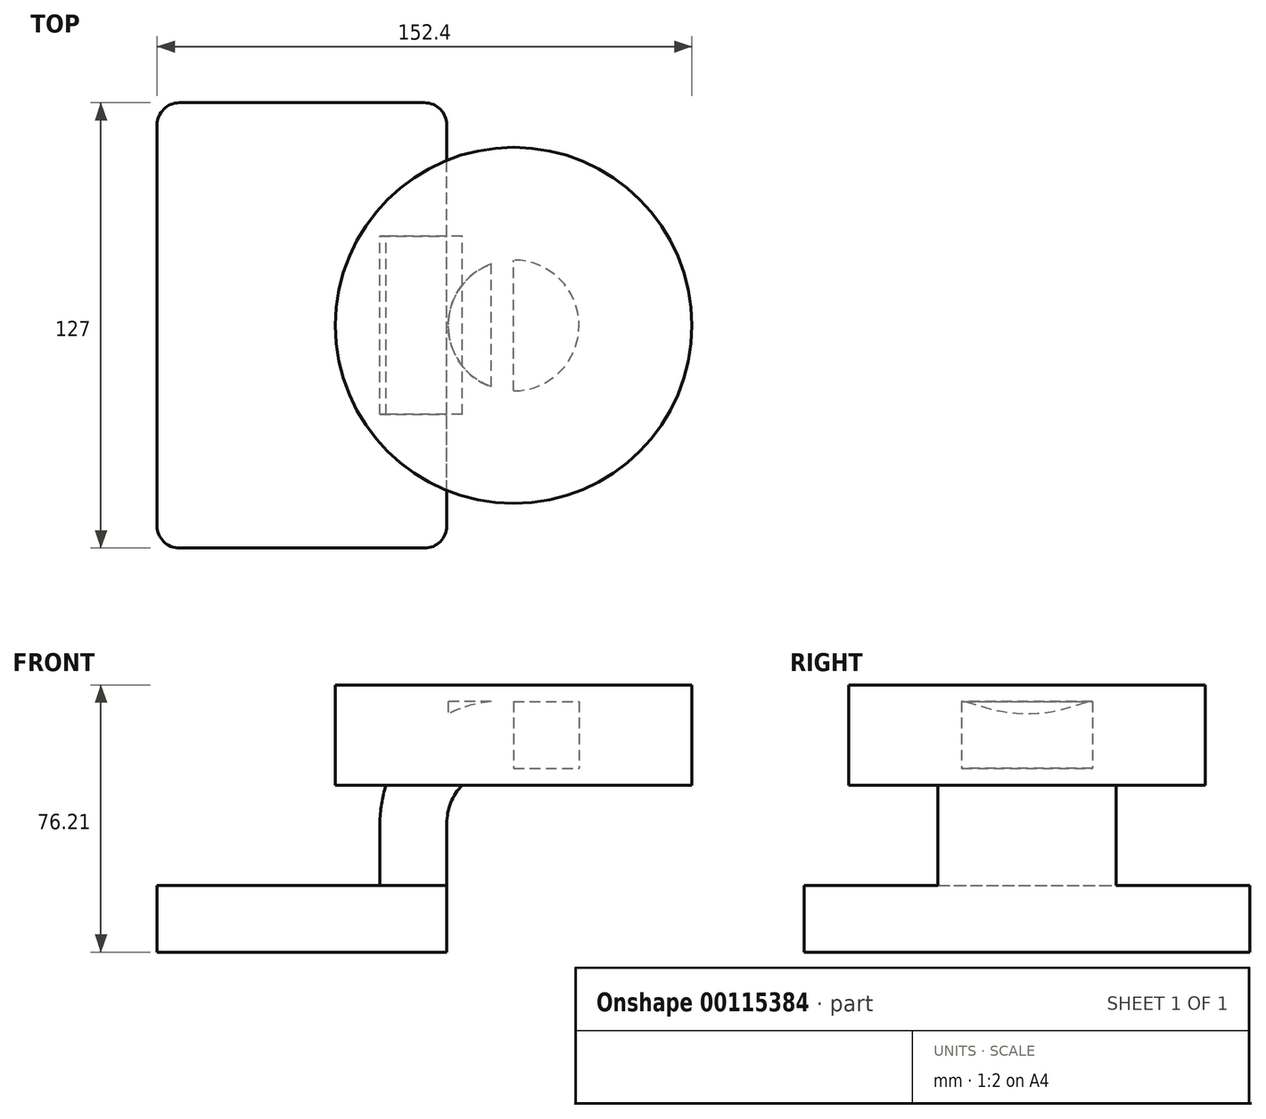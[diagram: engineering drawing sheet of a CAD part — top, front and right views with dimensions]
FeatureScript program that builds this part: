
annotation { "Feature Type Name" : "Feature", "Feature Type Description" : "" }
export const myFeature = defineFeature(function(context is Context, id is Id, definition is map)
    precondition{}
    {
        {
            var Q0;
            Q0=qCreatedBy(makeId("Front.planeOp"),FACE);
            var sketch = newSketch(context, id + "F0", { "sketchPlane" : qUnion([Q0])});
            skLineSegment(sketch, "E0.bottom", {"start": v(-41.28, 9.52) * mm, "end": v(41.28, 9.53) * mm});
            skLineSegment(sketch, "E0.top", {"start": v(-41.28, -9.53) * mm, "end": v(41.28, -9.53) * mm});
            skLineSegment(sketch, "E0.left", {"start": v(-41.28, 9.52) * mm, "end": v(-41.28, -9.53) * mm});
            skLineSegment(sketch, "E0.right", {"start": v(41.28, 9.53) * mm, "end": v(41.28, -9.52) * mm});
            skPoint(sketch, "E0.middle", {"position": v(0, 0) * mm});
            skLineSegment(sketch, "E1.bottom", {"start": v(111.12, 38.1) * mm, "end": v(60.32, 38.1) * mm});
            skLineSegment(sketch, "E1.top", {"start": v(111.12, 66.68) * mm, "end": v(60.32, 66.68) * mm});
            skLineSegment(sketch, "E1.left", {"start": v(111.12, 38.1) * mm, "end": v(111.12, 66.68) * mm});
            skLineSegment(sketch, "E1.right", {"start": v(60.32, 38.1) * mm, "end": v(60.32, 66.68) * mm});
            skPoint(sketch, "E1.middle", {"position": v(85.72, 52.39) * mm});
            skLineSegment(sketch, "E2", {"start": v(41.27, 9.53) * mm, "end": v(41.27, 27.15) * mm});
            skArc(sketch, "E3", {"start": v(41.27, 27.15) * mm, "mid": v(45.19, 37.58) * mm, "end": v(55, 42.88) * mm});
            skLineSegment(sketch, "E4", {"start": v(55, 42.88) * mm, "end": v(78.97, 42.88) * mm});
            skLineSegment(sketch, "E5.0", {"start": v(53.95, 61.93) * mm, "end": v(78.97, 61.93) * mm});
            skArc(sketch, "E5.1", {"start": v(22.22, 27.15) * mm, "mid": v(31.35, 50.68) * mm, "end": v(53.95, 61.93) * mm});
            skLineSegment(sketch, "E5.2", {"start": v(22.22, 9.53) * mm, "end": v(22.22, 27.15) * mm});
            skLineSegment(sketch, "E6", {"start": v(78.97, 42.88) * mm, "end": v(78.97, 61.93) * mm});
            skFitSpline(sketch, "E7", {"points": [v(-41.28, 9.52) * mm, v(53.95, 61.93) * mm], "startDerivative": vector(3.25, 108.48) * mm, "endDerivative": vector(161.85, 0) * mm});
            skSolve(sketch);
        }
        {
            var Q0;
            Q0=makeQuery(id+"F0.imprint","IMPRINT",FACE,{"disambiguationData":[TD([[makeQuery(id+"F0.imprint","IMPRINT",EDGE,{"derivedFrom":sQuery(id+"F0.wireOp",EDGE,"E0.top")}),1.0]])]});
            extrude(context, id + "F1", {"entities" : qUnion([Q0]), "endBound" : BoundingType.SYMMETRIC, "depth" : 127 * mm});
        }
        {
            var Q0;
            {var subQ1=sQuery(id+"F0.wireOp",EDGE,"E2");Q0=makeQuery(id+"F0.imprint","IMPRINT",FACE,{"disambiguationData":[TD([[makeQuery(id+"F0.imprint","IMPRINT",EDGE,{"derivedFrom":subQ1}),1.0]])]});}
            extrude(context, id + "F2", {"entities" : qUnion([Q0]), "operationType" : NewBodyOperationType.ADD, "endBound" : BoundingType.SYMMETRIC, "depth" : 50.8 * mm});
        }
        {
            var Q0;
            Q0=makeQuery(id+"F0.imprint","IMPRINT",FACE,{"disambiguationData":[TD([[makeQuery(id+"F0.imprint","IMPRINT",EDGE,{"derivedFrom":sQuery(id+"F0.wireOp",EDGE,"E5.1")}),1.0]])]});
            extrude(context, id + "F3", {"entities" : qUnion([Q0]), "operationType" : NewBodyOperationType.ADD, "endBound" : BoundingType.SYMMETRIC, "depth" : 15.88 * mm});
        }
        {
            var Q0;
            {var subQ1=sQuery(id+"F0.wireOp",EDGE,"E1.bottom");Q0=makeQuery(id+"F0.imprint","IMPRINT",FACE,{"disambiguationData":[TD([[makeQuery(id+"F0.imprint","IMPRINT",EDGE,{"derivedFrom":subQ1}),-1.0]])]});}
            var Q1;
            Q1=sQuery(id+"F0.wireOp",EDGE,"E1.right");
            revolve(context, id + "F4", {"operationType" : NewBodyOperationType.ADD, "entities" : qUnion([Q0]), "axis" : qUnion([Q1]), "revolveType" : RevolveType.FULL});
        }
        {
            var Q0;
            Q0=makeQuery(id+"F1.opExtrude","CAP_EDGE",EDGE,{"disambiguationData":[OSD([sQuery(id+"F0.wireOp",EDGE,"E0.left")])],"isStart":false});
            var Q1;
            Q1=makeQuery(id+"F1.opExtrude","CAP_EDGE",EDGE,{"disambiguationData":[OSD([sQuery(id+"F0.wireOp",EDGE,"E0.right")])],"isStart":false});
            var Q2;
            Q2=makeQuery(id+"F1.opExtrude","CAP_EDGE",EDGE,{"disambiguationData":[OSD([sQuery(id+"F0.wireOp",EDGE,"E0.right")])],"isStart":true});
            var Q3;
            Q3=makeQuery(id+"F1.opExtrude","CAP_EDGE",EDGE,{"disambiguationData":[OSD([sQuery(id+"F0.wireOp",EDGE,"E0.left")])],"isStart":true});
            fillet(context, id + "F5", {"entities" : qUnion([Q0, Q1, Q2, Q3]), "radius" : 6.35 * mm, "tangentPropagation" : true, "allowEdgeOverflow" : false});
        }
    });
